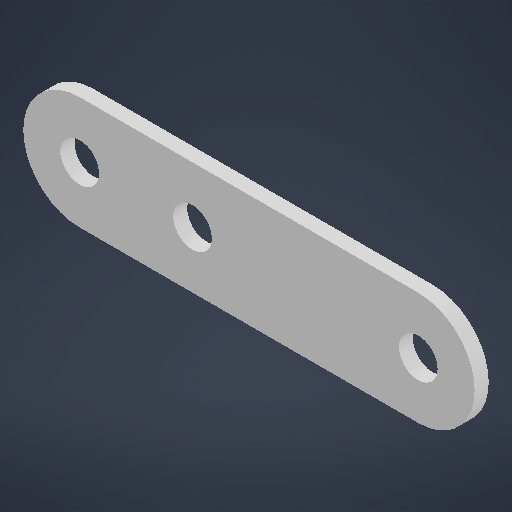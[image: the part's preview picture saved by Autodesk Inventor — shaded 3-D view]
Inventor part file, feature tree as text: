
AUTODESK INVENTOR PART (.ipt)
format: ipt  version: 2025.2 (Build 292293000, 293)  size: 178,688 bytes
history: native  units: in
note: dims shown in document units (in); Inventor stores cm internally (conversion verified against a paired STEP export)
features: extrude x1, sketch x1
ambient origin geometry x8: Origin, YZ Plane, XZ Plane, XY Plane, X Axis, Y Axis, Z Axis, Center Point
bodies: Solid1 (feature_tree)
feature tree (2):
  extrude  "Extrusion1"  Depth=0.0625in
  sketch  "Sketch1"  dims[d0=0.172in d2=0.172in d5=0.0625in d6=0.0in d8=0.172in]
